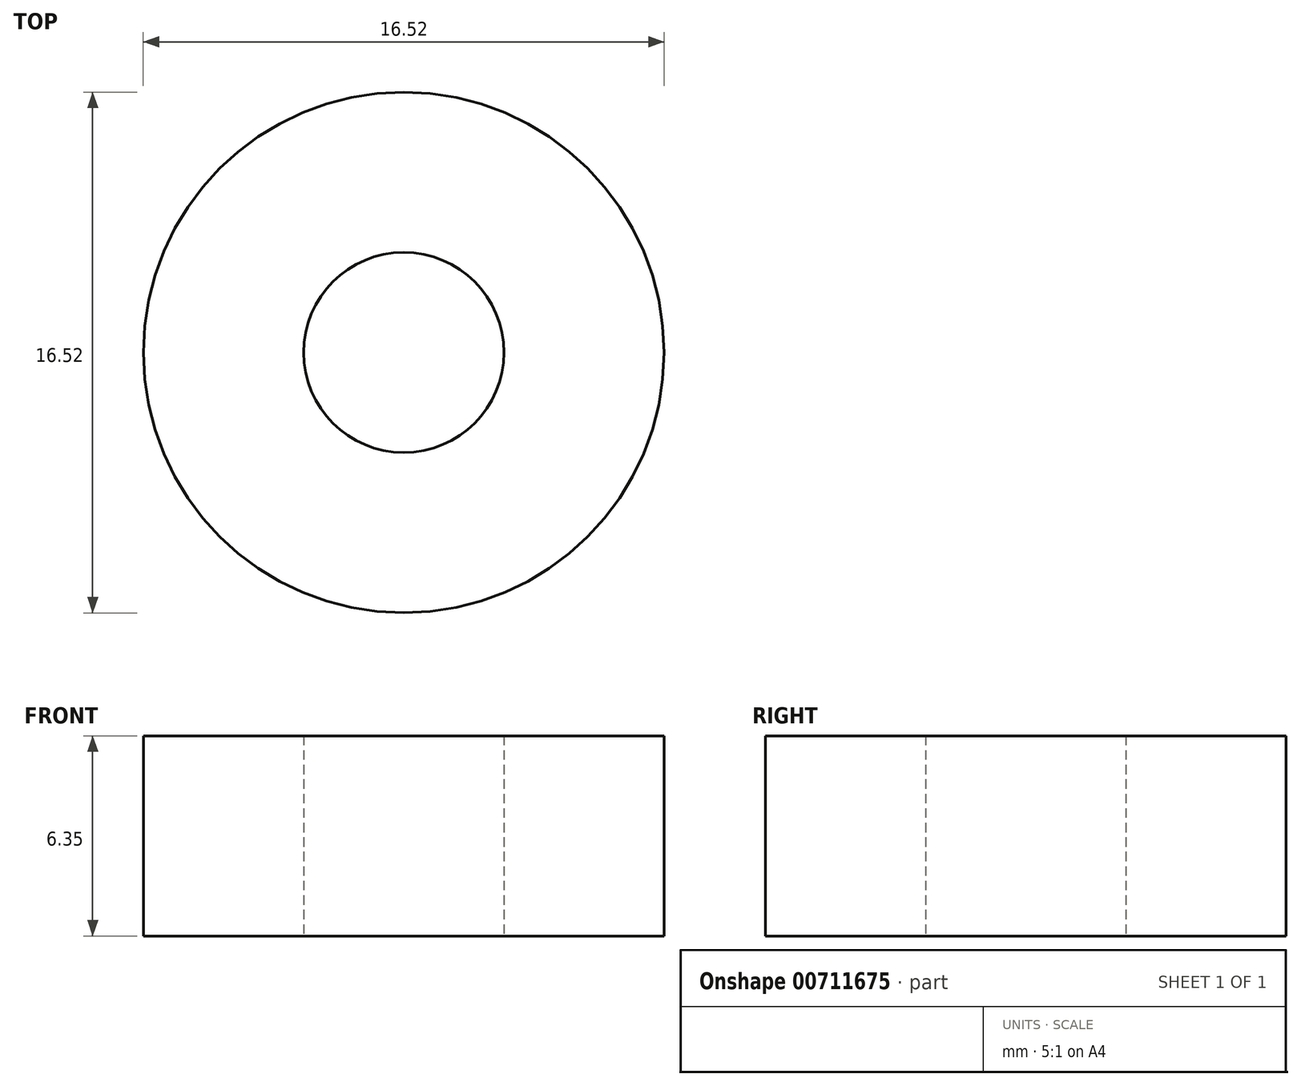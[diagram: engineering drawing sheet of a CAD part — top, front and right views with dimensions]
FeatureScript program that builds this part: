
annotation { "Feature Type Name" : "Feature", "Feature Type Description" : "" }
export const myFeature = defineFeature(function(context is Context, id is Id, definition is map)
    precondition{}
    {
        {
            var Q0;
            Q0=qCreatedBy(makeId("Top.planeOp"),FACE);
            var sketch = newSketch(context, id + "F0", { "sketchPlane" : qUnion([Q0])});
            skCircle(sketch, "E0", {"center": v(0, 0) * mm, "radius": 3.18 * mm});
            skCircle(sketch, "E1", {"center": v(0, 0) * mm, "radius": 8.26 * mm});
            skSolve(sketch);
        }
        {
            var Q0;
            Q0 = qSketchRegion(id + "F0", true);
            extrude(context, id + "F1", {"entities" : qUnion([Q0]), "depth" : 6.35 * mm, "offsetDistance" : 25.4 * mm});
        }
    });
